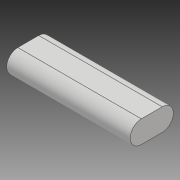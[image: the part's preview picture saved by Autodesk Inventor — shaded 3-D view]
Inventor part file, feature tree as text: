
AUTODESK INVENTOR PART (.ipt)
format: ipt  version: 2018 (Build 220112000, 112)  size: 79,872 bytes
history: native  units: mm
features: other x1, extrude x1, sketch x1
ambient origin geometry x8: Origin, YZ Plane, XZ Plane, XY Plane, X Axis, Y Axis, Z Axis, Center Point
bodies: Body1 (feature_tree)
feature tree (3):
  other  "ソリッド1"
  extrude  "押し出し1"  Depth=24.5mm
  sketch  "スケッチ1"
